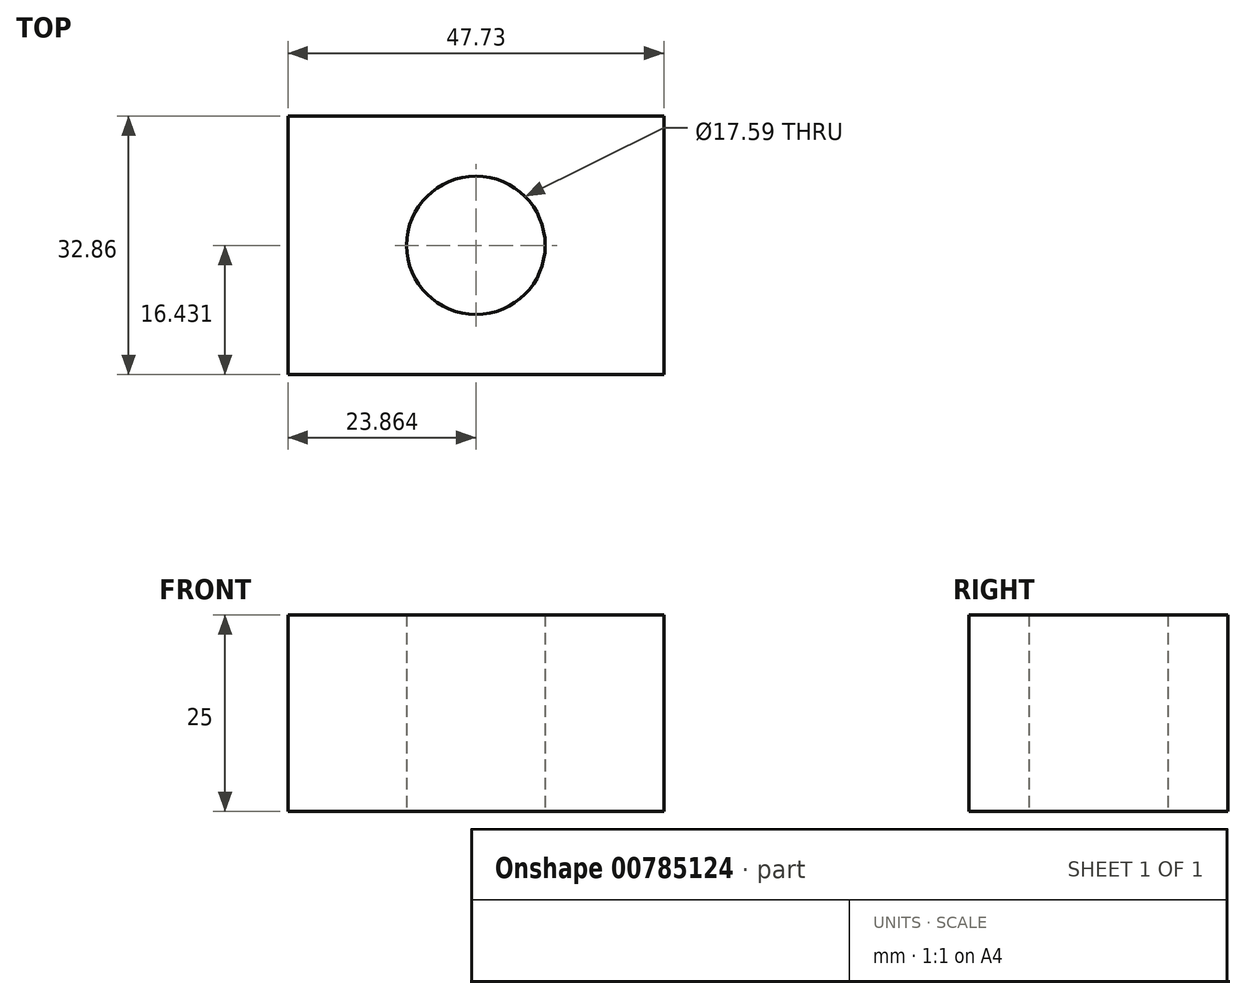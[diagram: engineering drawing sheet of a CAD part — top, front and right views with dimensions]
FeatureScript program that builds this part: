
annotation { "Feature Type Name" : "Feature", "Feature Type Description" : "" }
export const myFeature = defineFeature(function(context is Context, id is Id, definition is map)
    precondition{}
    {
        {
            var Q0;
            Q0=qCreatedBy(makeId("Top.planeOp"),FACE);
            var sketch = newSketch(context, id + "F0", { "sketchPlane" : qUnion([Q0])});
            skLineSegment(sketch, "E0.bottom", {"start": v(0, 33.85) * mm, "end": v(-47.73, 33.85) * mm});
            skLineSegment(sketch, "E0.top", {"start": v(0, 66.71) * mm, "end": v(-47.73, 66.71) * mm});
            skLineSegment(sketch, "E0.left", {"start": v(0, 33.85) * mm, "end": v(0, 66.71) * mm});
            skLineSegment(sketch, "E0.right", {"start": v(-47.73, 33.85) * mm, "end": v(-47.73, 66.71) * mm});
            skPoint(sketch, "E0.middle", {"position": v(-23.87, 50.28) * mm});
            skCircle(sketch, "E1", {"center": v(-23.87, 50.28) * mm, "radius": 8.8 * mm});
            skSolve(sketch);
        }
        {
            var Q0;
            Q0=makeQuery(id+"F0.imprint","IMPRINT",FACE,{"disambiguationData":[TD([[makeQuery(id+"F0.imprint","IMPRINT",EDGE,{"derivedFrom":sQuery(id+"F0.wireOp",EDGE,"E0.bottom")}),-1.0]])]});
            extrude(context, id + "F1", {"entities" : qUnion([Q0]), "depth" : 25 * mm, "offsetDistance" : 25 * mm});
        }
    });
